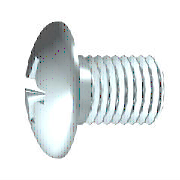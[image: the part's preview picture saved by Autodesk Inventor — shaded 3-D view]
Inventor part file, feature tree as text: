
AUTODESK INVENTOR PART (.ipt)
format: ipt  version: 2025 (Build 290162000, 162)  size: 270,848 bytes
history: native  units: mm (DEFAULTED — no unit token found)
features: plane x1, extrude x1, other x1
ambient origin geometry x7: Origin, YZ Plane, XZ Plane, X Axis, Y Axis, Z Axis, Center Point
bodies: Solid1 (feature_tree), Body (feature_tree)
feature tree (3):
  plane  "Workplane"
  extrude  "Slot"  Depth=4.0mm
  other  "Cut"
